# Revit family: ITK_Розетка информационная GENERICA категория 3_Настенная_1 порт_IP20
name_source: partatom
category: Обобщенные модели
units: mm (PartAtom-declared; Revit-internal decimal feet)

## family parameters
Всегда вертикально = Да
Может служить основой для арматурных стержней = Нет
На основе рабочей плоскости = Нет
Общий = Нет
При загрузке вырезать с полостями = Нет
Размер круглого соединителя = Использовать диаметр
Тип детали = Нормальный
Точка расчета площади = Нет

## types (1)
- Категория3_UTP
    ADSK_URL страницы изделия = https://generica.su
    ADSK_Версия Revit = 2019
    ADSK_Версия семейства = 1.0
    ADSK_Группирование = I. ЩИТЫ И ПУЛЬТЫ
    ADSK_Единица измерения = шт
    ADSK_Завод-изготовитель = IEK
    ADSK_Код изделия = CS2-3C03U-12-G
    ADSK_Масса = 0
    ADSK_Материал наименование = АБС-пластик
    ADSK_Наименование = Розетка инф. настенная RJ12 кат. 3 UTP 1 порт GENERICA
    IEK_URL = https://generica.su
    IEK_Описание = Используется для подключения оконечного оборудования пользователей на рабочих местах к информационной сети.
    IEK_Цена за единицу = 44.77
    KSI_CMa_Строительные материалы = 01.7.14.03
    URL = https://www.iek.ru
    Высота = 24 мм
    Глубина = 58 мм
    Изготовитель = ITK
    Материал = Пластик белый
    Степень защиты = IP20
    Ширина = 42 мм
